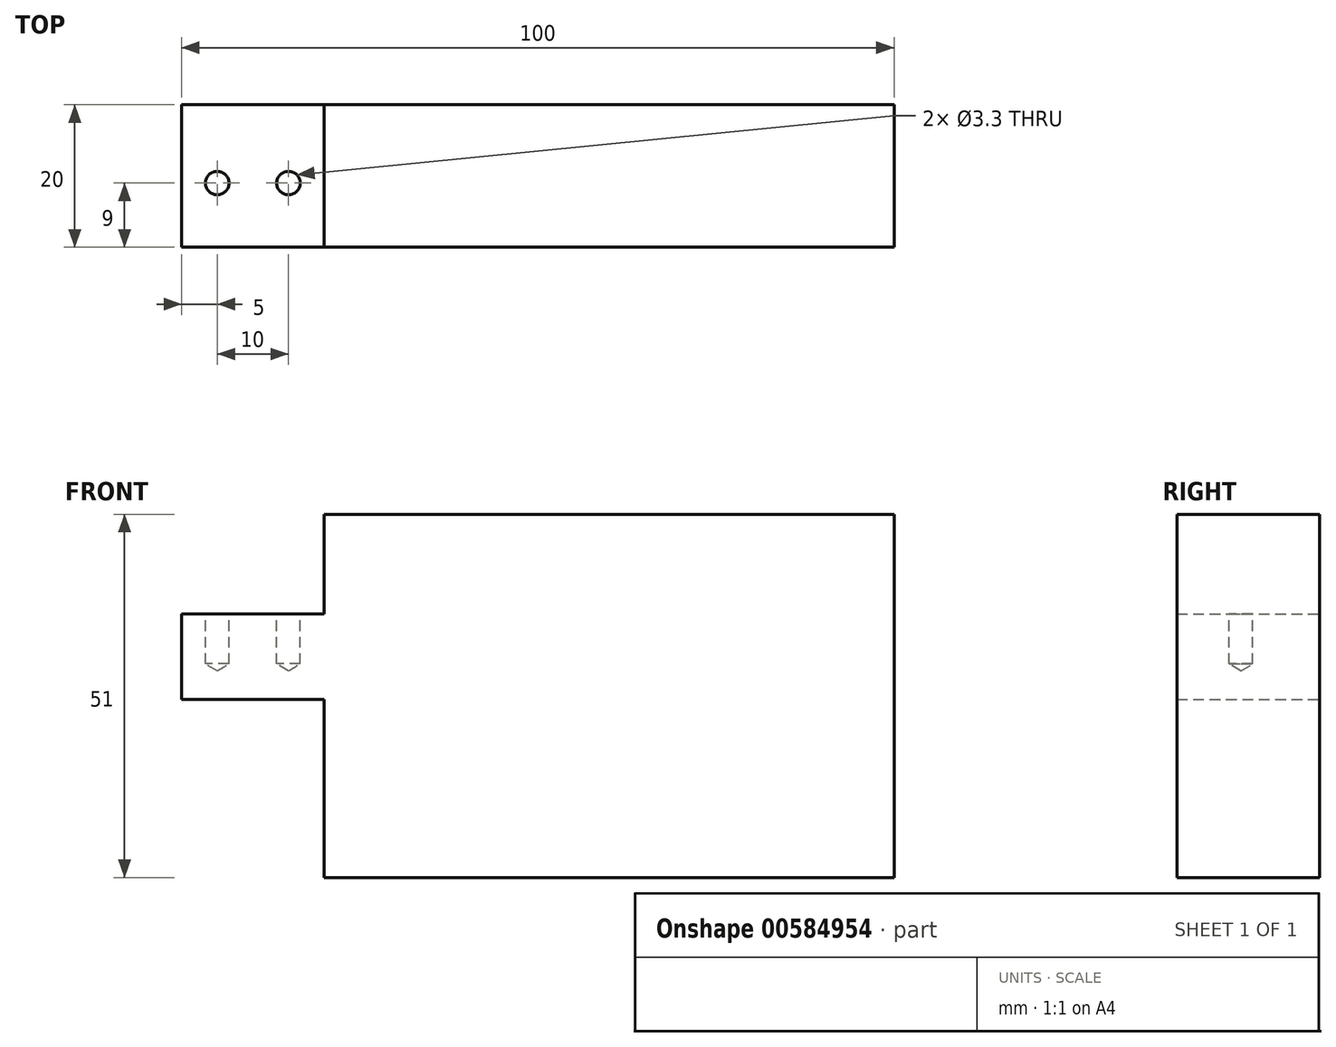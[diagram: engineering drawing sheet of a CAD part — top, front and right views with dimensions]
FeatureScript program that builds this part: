
annotation { "Feature Type Name" : "Feature", "Feature Type Description" : "" }
export const myFeature = defineFeature(function(context is Context, id is Id, definition is map)
    precondition{}
    {
        {
            var Q0;
            Q0=qCreatedBy(makeId("Top.planeOp"),FACE);
            var sketch = newSketch(context, id + "F0", { "sketchPlane" : qUnion([Q0])});
            skLineSegment(sketch, "E0.bottom", {"start": v(0, 0) * mm, "end": v(100, 0) * mm});
            skLineSegment(sketch, "E0.top", {"start": v(0, 20) * mm, "end": v(100, 20) * mm});
            skLineSegment(sketch, "E0.left", {"start": v(0, 0) * mm, "end": v(0, 20) * mm});
            skLineSegment(sketch, "E0.right", {"start": v(100, 0) * mm, "end": v(100, 20) * mm});
            skSolve(sketch);
        }
        {
            var Q0;
            Q0 = qSketchRegion(id + "F0", true);
            extrude(context, id + "F1", {"entities" : qUnion([Q0]), "depth" : 51 * mm, "offsetDistance" : 25 * mm});
        }
        {
            var Q0;
            Q0=makeQuery(id+"F1.opExtrude","CAP_FACE",FACE,{"disambiguationData":[OSD([sQuery(id+"F0.wireOp",EDGE,"E0.bottom"),sQuery(id+"F0.wireOp",EDGE,"E0.top"),sQuery(id+"F0.wireOp",EDGE,"E0.left"),sQuery(id+"F0.wireOp",EDGE,"E0.right")])],"isStart":false});
            var sketch = newSketch(context, id + "F2", { "sketchPlane" : qUnion([Q0])});
            skLineSegment(sketch, "E1.bottom", {"start": v(0, 20) * mm, "end": v(20, 20) * mm});
            skLineSegment(sketch, "E1.top", {"start": v(0, 0) * mm, "end": v(20, 0) * mm});
            skLineSegment(sketch, "E1.left", {"start": v(0, 20) * mm, "end": v(0, 0) * mm});
            skLineSegment(sketch, "E1.right", {"start": v(20, 20) * mm, "end": v(20, 0) * mm});
            skSolve(sketch);
        }
        {
            var Q0;
            Q0 = qSketchRegion(id + "F2", true);
            extrude(context, id + "F3", {"entities" : qUnion([Q0]), "operationType" : NewBodyOperationType.REMOVE, "oppositeDirection" : true, "depth" : 14 * mm, "offsetDistance" : 25 * mm});
        }
        {
            var Q0;
            Q0=makeQuery(id+"F3.boolean.opBoolean","COPY",FACE,{"derivedFrom":makeQuery(id+"F3.opExtrude","CAP_FACE",FACE,{"disambiguationData":[OSD([sQuery(id+"F2.wireOp",EDGE,"E1.bottom"),sQuery(id+"F2.wireOp",EDGE,"E1.top"),sQuery(id+"F2.wireOp",EDGE,"E1.left"),sQuery(id+"F2.wireOp",EDGE,"E1.right")])],"isStart":false})});
            var sketch = newSketch(context, id + "F4", { "sketchPlane" : qUnion([Q0])});
            skPoint(sketch, "E2", {"position": v(5, 9) * mm});
            skPoint(sketch, "E3", {"position": v(15, 9) * mm});
            skLineSegment(sketch, "E4", {"start": v(5, 9) * mm, "end": v(15, 9) * mm, "construction": true});
            skSolve(sketch);
        }
        {
            var Q0;
            Q0=sQuery(id+"F4.wireOp",VERTEX,"E2");
            var Q1;
            Q1=sQuery(id+"F4.wireOp",VERTEX,"E3");
            var Q2;
            Q2=makeQuery(id+"F1.opExtrude","SWEPT_BODY",BODY,{"disambiguationData":[OSD([sQuery(id+"F0.wireOp",EDGE,"E0.bottom"),sQuery(id+"F0.wireOp",EDGE,"E0.top"),sQuery(id+"F0.wireOp",EDGE,"E0.left"),sQuery(id+"F0.wireOp",EDGE,"E0.right")])]});
            hole(context, id + "F5", {"style" : HoleStyle.SIMPLE, "endStyle" : HoleEndStyle.BLIND, "standardTappedOrClearance" : lookupTablePath({ "standard" : "ISO", "fit" : "Normal", "size" : "M3", "type" : "Clearance" }), "standardBlindInLast" : lookupTablePath({ "fit" : "Standard", "standard" : "ISO", "size" : "M3", "type" : "Clearance" }), "holeDiameter" : 3.3 * mm, "majorDiameter" : 5 * mm, "holeDepth" : 7 * mm, "isTappedThrough" : true, "tappedDepth" : 7 * mm, "tapClearance" : 2, "startFromSketch" : true, "locations" : qUnion([Q0, Q1]), "scope" : qUnion([Q2])});
        }
        {
            var Q0;
            Q0=makeQuery(id+"F1.opExtrude","CAP_FACE",FACE,{"disambiguationData":[OSD([sQuery(id+"F0.wireOp",EDGE,"E0.bottom"),sQuery(id+"F0.wireOp",EDGE,"E0.top"),sQuery(id+"F0.wireOp",EDGE,"E0.left"),sQuery(id+"F0.wireOp",EDGE,"E0.right")])],"isStart":true});
            var sketch = newSketch(context, id + "F6", { "sketchPlane" : qUnion([Q0])});
            skLineSegment(sketch, "E5.bottom", {"start": v(0, 0) * mm, "end": v(20, 0) * mm});
            skLineSegment(sketch, "E5.top", {"start": v(0, -20) * mm, "end": v(20, -20) * mm});
            skLineSegment(sketch, "E5.left", {"start": v(0, 0) * mm, "end": v(0, -20) * mm});
            skLineSegment(sketch, "E5.right", {"start": v(20, 0) * mm, "end": v(20, -20) * mm});
            skSolve(sketch);
        }
        {
            var Q0;
            Q0=makeQuery(id+"F6.imprint","IMPRINT",FACE,{"disambiguationData":[TD([[makeQuery(id+"F6.imprint","IMPRINT",EDGE,{"derivedFrom":sQuery(id+"F6.wireOp",EDGE,"E5.bottom")}),-1.0]])]});
            extrude(context, id + "F7", {"entities" : qUnion([Q0]), "operationType" : NewBodyOperationType.REMOVE, "oppositeDirection" : true, "depth" : 25 * mm, "offsetDistance" : 25 * mm});
        }
    });
